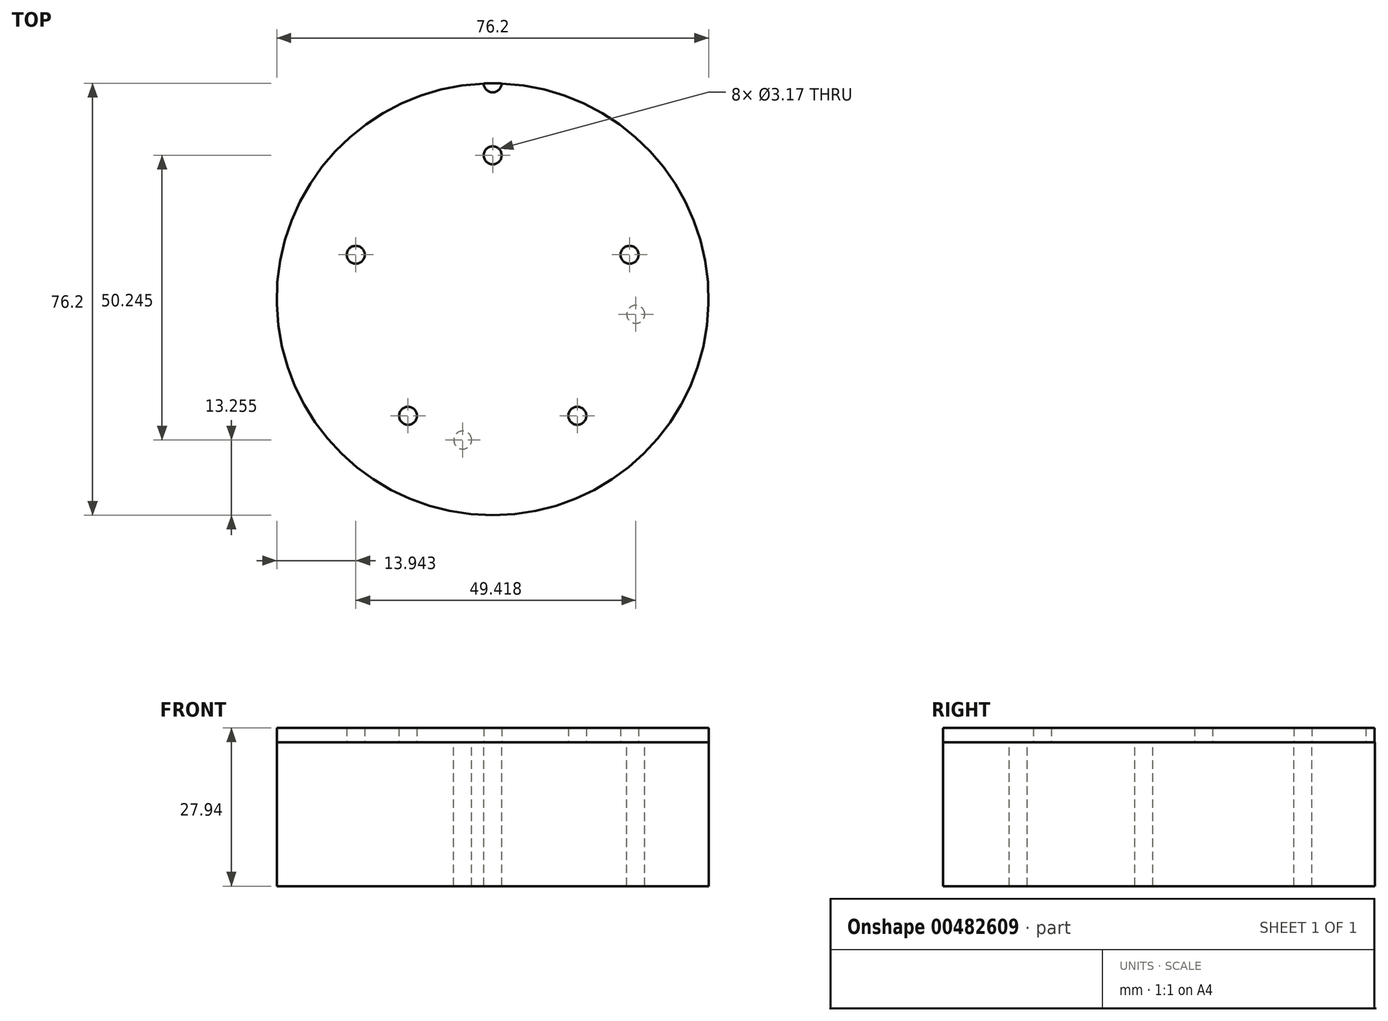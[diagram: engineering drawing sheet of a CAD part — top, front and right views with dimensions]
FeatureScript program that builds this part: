
annotation { "Feature Type Name" : "Feature", "Feature Type Description" : "" }
export const myFeature = defineFeature(function(context is Context, id is Id, definition is map)
    precondition{}
    {
        {
            var Q0;
            Q0=qCreatedBy(makeId("Top.planeOp"),FACE);
            var sketch = newSketch(context, id + "F0", { "sketchPlane" : qUnion([Q0])});
            skCircle(sketch, "E0", {"center": v(0, 0) * mm, "radius": 38.1 * mm});
            skCircle(sketch, "E1", {"center": v(0, 25.4) * mm, "radius": 1.59 * mm});
            skCircle(sketch, "E2.1.0", {"center": v(-10.33, 23.2) * mm, "radius": 1.59 * mm, "construction": true});
            skCircle(sketch, "E2.2.0", {"center": v(-18.88, 17) * mm, "radius": 1.59 * mm, "construction": true});
            skCircle(sketch, "E3.1.3.0", {"center": v(-24.16, 7.85) * mm, "radius": 1.59 * mm});
            skCircle(sketch, "E3.1.4.0", {"center": v(-25.26, -2.66) * mm, "radius": 1.59 * mm, "construction": true});
            skCircle(sketch, "E4.1.5.0", {"center": v(-22, -12.7) * mm, "radius": 1.59 * mm, "construction": true});
            skCircle(sketch, "E4.1.6.0", {"center": v(-14.93, -20.55) * mm, "radius": 1.59 * mm});
            skCircle(sketch, "E4.1.7.0", {"center": v(-5.28, -24.84) * mm, "radius": 1.59 * mm, "construction": true});
            skCircle(sketch, "E4.1.8.0", {"center": v(5.28, -24.84) * mm, "radius": 1.59 * mm, "construction": true});
            skCircle(sketch, "E4.1.9.0", {"center": v(14.93, -20.55) * mm, "radius": 1.59 * mm});
            skCircle(sketch, "E4.1.10.0", {"center": v(22, -12.7) * mm, "radius": 1.59 * mm, "construction": true});
            skCircle(sketch, "E4.1.11.0", {"center": v(25.26, -2.66) * mm, "radius": 1.59 * mm, "construction": true});
            skCircle(sketch, "E4.1.12.0", {"center": v(24.16, 7.85) * mm, "radius": 1.59 * mm});
            skCircle(sketch, "E4.1.13.0", {"center": v(18.88, 17) * mm, "radius": 1.59 * mm, "construction": true});
            skCircle(sketch, "E4.1.14.0", {"center": v(10.33, 23.2) * mm, "radius": 1.59 * mm, "construction": true});
            skCircle(sketch, "E5", {"center": v(0, 38.1) * mm, "radius": 1.59 * mm});
            skSolve(sketch);
        }
        {
            var Q0;
            Q0=qCreatedBy(makeId("Top.planeOp"),FACE);
            var sketch = newSketch(context, id + "F1", { "sketchPlane" : qUnion([Q0])});
            skCircle(sketch, "E6.0", {"center": v(0, 0) * mm, "radius": 38.1 * mm});
            skCircle(sketch, "E7.0", {"center": v(0, 25.4) * mm, "radius": 1.59 * mm});
            skCircle(sketch, "E7.1", {"center": v(25.26, -2.66) * mm, "radius": 1.59 * mm});
            skCircle(sketch, "E7.2", {"center": v(-5.28, -24.84) * mm, "radius": 1.59 * mm});
            skSolve(sketch);
        }
        {
            var Q0;
            Q0=makeQuery(id+"F1.imprint","IMPRINT",FACE,{"disambiguationData":[TD([[makeQuery(id+"F1.imprint","IMPRINT",EDGE,{"derivedFrom":sQuery(id+"F1.wireOp",EDGE,"E6.0")}),1.0]])]});
            extrude(context, id + "F2", {"entities" : qUnion([Q0]), "oppositeDirection" : true, "depth" : 25.4 * mm});
        }
        {
            var Q0;
            Q0=makeQuery(id+"F0.imprint","IMPRINT",FACE,{"disambiguationData":[TD([[makeQuery(id+"F0.imprint","IMPRINT",EDGE,{"derivedFrom":sQuery(id+"F0.wireOp",EDGE,"E1")}),-1.0]])]});
            extrude(context, id + "F3", {"entities" : qUnion([Q0]), "depth" : 2.54 * mm});
        }
    });
